# Revit family: Screen_LargeOpening_ExecutiveSeries_PhantomScreens-1
name_source: partatom
category: Doors
units: mm (PartAtom-declared; Revit-internal decimal feet)

## family parameters
Always vertical = Yes
Cut with Voids When Loaded = No
Host = Wall
OmniClass Number = 23.30.60.21
OmniClass Title = Insect Screens
Room Calculation Point = No
Shared = No

## types (1)
- Type as Specified
    Assembly Code = B2020400
    Construction Details = http://www.arcat.com
    Description = Phantom Screens Executive Series Screen
    Frame Projection Ext. = 0' - 1"
    Frame Projection Int. = 0' - 1"
    Frame Width = 0' - 3"
    Function = Exterior
    Housing = Light Cherry
    Installation-Fabrication = http://www.phantomscreens.com
    Keynote = 08 11 00
    Manufacturer = Phantom Screens
    Manufacturer Fax = 604-855-7834
    Manufacturer Website = http://www.phantomscreens.com
    Model = Executive Series
    Product Data = http://www.arcat.com
    Product Properties = http://www.phantomscreens.com
    Revision = R1_08-2016
    Sales Information = http://www.phantomscreens.com
    Screen = Opaque - Black
    Screen Width = 0' - 0 1/8"
    Slide Bar = Light Cherry
    Slide Bar Height = 0' - 3 11/16"
    Slide Bar Width = 0' - 1 1/32"
    Specification = http://www.phantomscreens.com
    Track = Light Cherry
    Track Depth = 0' - 1 17/32"
    Track Width = 0' - 1 3/8"
    URL = http://www.phantomscreens.com
    Wall Closure = By host

## geometry (parser evidence)
native form markers: Sweep x3
no freeform markers — native parametric forms only
